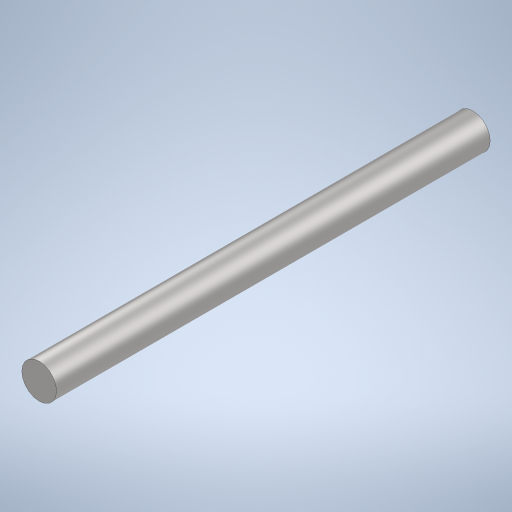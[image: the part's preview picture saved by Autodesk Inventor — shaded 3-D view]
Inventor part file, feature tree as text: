
AUTODESK INVENTOR PART (.ipt)
format: ipt  version: 2023.2 (Build 272271000, 271)  size: 246,272 bytes
history: native  units: mm
features: extrude x1, sketch x1
ambient origin geometry x8: Origin, YZ Plane, XZ Plane, XY Plane, X Axis, Y Axis, Z Axis, Center Point
bodies: Solid1 (feature_tree)
feature tree (2):
  extrude  "Extrusion1"  Depth=100.0mm TaperAngle=0.0deg
  sketch  "Sketch1"  dims[d0=8.0mm d1=100.0mm d2=0.0mm]
